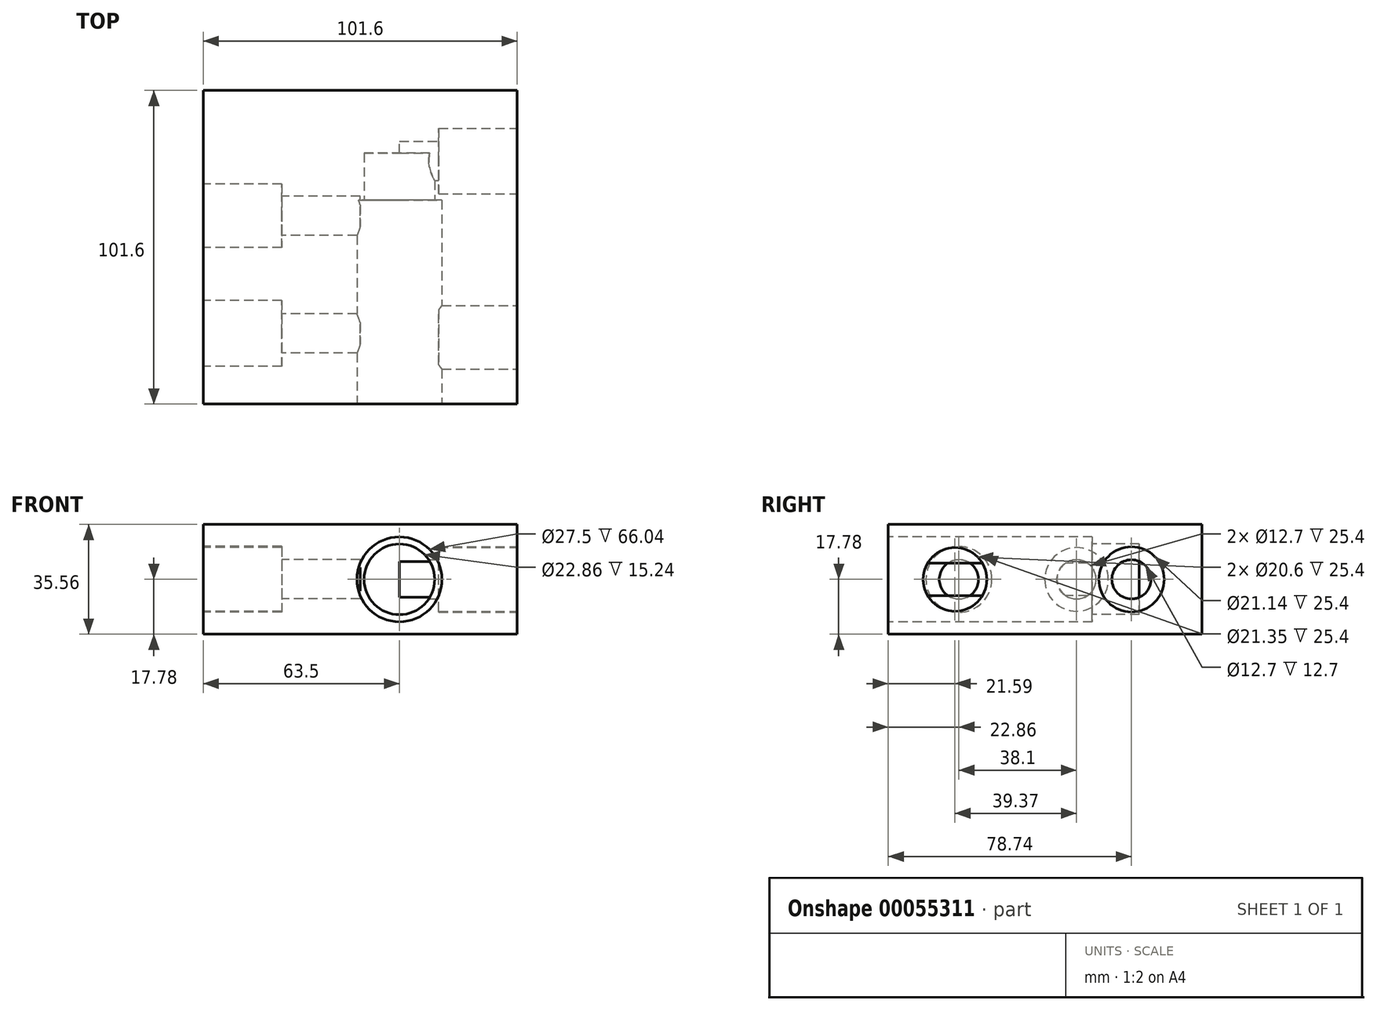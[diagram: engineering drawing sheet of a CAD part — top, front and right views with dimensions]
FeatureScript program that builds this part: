
annotation { "Feature Type Name" : "Feature", "Feature Type Description" : "" }
export const myFeature = defineFeature(function(context is Context, id is Id, definition is map)
    precondition{}
    {
        {
            var Q0;
            Q0=qCreatedBy(makeId("Top.planeOp"),FACE);
            var sketch = newSketch(context, id + "F0", { "sketchPlane" : qUnion([Q0])});
            skLineSegment(sketch, "E0.bottom", {"start": v(0, 0) * mm, "end": v(101.6, 0) * mm});
            skLineSegment(sketch, "E0.top", {"start": v(0, 101.6) * mm, "end": v(101.6, 101.6) * mm});
            skLineSegment(sketch, "E0.left", {"start": v(0, 0) * mm, "end": v(0, 101.6) * mm});
            skLineSegment(sketch, "E0.right", {"start": v(101.6, 0) * mm, "end": v(101.6, 101.6) * mm});
            skSolve(sketch);
        }
        {
            var Q0;
            Q0=makeQuery(id+"F0.imprint","IMPRINT",FACE,{"disambiguationData":[TD([[makeQuery(id+"F0.imprint","IMPRINT",EDGE,{"derivedFrom":sQuery(id+"F0.wireOp",EDGE,"E0.bottom")}),1.0]])]});
            extrude(context, id + "F1", {"entities" : qUnion([Q0]), "depth" : 35.56 * mm});
        }
        {
            var Q0;
            Q0=makeQuery(id+"F1.opExtrude","SWEPT_FACE",FACE,{"disambiguationData":[OSD([sQuery(id+"F0.wireOp",EDGE,"E0.bottom")])]});
            var sketch = newSketch(context, id + "F2", { "sketchPlane" : qUnion([Q0])});
            skCircle(sketch, "E1", {"center": v(63.5, 17.78) * mm, "radius": 13.75 * mm});
            skCircle(sketch, "E2", {"center": v(63.5, 17.78) * mm, "radius": 11.43 * mm});
            skSolve(sketch);
        }
        {
            var Q0;
            Q0=makeQuery(id+"F1.opExtrude","SWEPT_FACE",FACE,{"disambiguationData":[OSD([sQuery(id+"F0.wireOp",EDGE,"E0.left")])]});
            var sketch = newSketch(context, id + "F3", { "sketchPlane" : qUnion([Q0])});
            skCircle(sketch, "E3", {"center": v(-60.96, 17.78) * mm, "radius": 10.3 * mm});
            skCircle(sketch, "E4", {"center": v(-22.86, 17.78) * mm, "radius": 10.68 * mm});
            skCircle(sketch, "E5", {"center": v(-60.96, 17.78) * mm, "radius": 6.35 * mm});
            skCircle(sketch, "E6", {"center": v(-22.86, 17.78) * mm, "radius": 6.35 * mm});
            skSolve(sketch);
        }
        {
            var Q0;
            Q0=makeQuery(id+"F1.opExtrude","SWEPT_FACE",FACE,{"disambiguationData":[OSD([sQuery(id+"F0.wireOp",EDGE,"E0.right")])]});
            var sketch = newSketch(context, id + "F4", { "sketchPlane" : qUnion([Q0])});
            skCircle(sketch, "E7", {"center": v(21.59, 17.78) * mm, "radius": 10.3 * mm});
            skCircle(sketch, "E8", {"center": v(78.74, 17.78) * mm, "radius": 10.57 * mm});
            skCircle(sketch, "E9", {"center": v(78.74, 17.78) * mm, "radius": 6.35 * mm});
            skSolve(sketch);
        }
        {
            var Q0;
            Q0=makeQuery(id+"F2.imprint","IMPRINT",FACE,{"disambiguationData":[TD([[makeQuery(id+"F2.imprint","IMPRINT",EDGE,{"derivedFrom":sQuery(id+"F2.wireOp",EDGE,"E1")}),1.0]])]});
            var Q1;
            Q1=makeQuery(id+"F2.imprint","IMPRINT",FACE,{"disambiguationData":[TD([[makeQuery(id+"F2.imprint","IMPRINT",EDGE,{"derivedFrom":sQuery(id+"F2.wireOp",EDGE,"E2")}),1.0]])]});
            extrude(context, id + "F5", {"entities" : qUnion([Q0, Q1]), "operationType" : NewBodyOperationType.REMOVE, "oppositeDirection" : true, "depth" : 66.04 * mm});
        }
        {
            var Q0;
            Q0=makeQuery(id+"F2.imprint","IMPRINT",FACE,{"disambiguationData":[TD([[makeQuery(id+"F2.imprint","IMPRINT",EDGE,{"derivedFrom":sQuery(id+"F2.wireOp",EDGE,"E2")}),1.0]])]});
            extrude(context, id + "F6", {"entities" : qUnion([Q0]), "operationType" : NewBodyOperationType.REMOVE, "oppositeDirection" : true, "depth" : 81.28 * mm});
        }
        {
            var Q0;
            Q0=makeQuery(id+"F4.imprint","IMPRINT",FACE,{"disambiguationData":[TD([[makeQuery(id+"F4.imprint","IMPRINT",EDGE,{"derivedFrom":sQuery(id+"F4.wireOp",EDGE,"E7")}),1.0]])]});
            var Q1;
            Q1=makeQuery(id+"F4.imprint","IMPRINT",FACE,{"disambiguationData":[TD([[makeQuery(id+"F4.imprint","IMPRINT",EDGE,{"derivedFrom":sQuery(id+"F4.wireOp",EDGE,"E8")}),1.0]])]});
            extrude(context, id + "F7", {"entities" : qUnion([Q0, Q1]), "operationType" : NewBodyOperationType.REMOVE, "oppositeDirection" : true, "depth" : 25.4 * mm});
        }
        {
            var Q0;
            Q0=makeQuery(id+"F3.imprint","IMPRINT",FACE,{"disambiguationData":[TD([[makeQuery(id+"F3.imprint","IMPRINT",EDGE,{"derivedFrom":sQuery(id+"F3.wireOp",EDGE,"E5")}),1.0]])]});
            var Q1;
            Q1=makeQuery(id+"F3.imprint","IMPRINT",FACE,{"disambiguationData":[TD([[makeQuery(id+"F3.imprint","IMPRINT",EDGE,{"derivedFrom":sQuery(id+"F3.wireOp",EDGE,"E6")}),1.0]])]});
            extrude(context, id + "F8", {"entities" : qUnion([Q0, Q1]), "operationType" : NewBodyOperationType.REMOVE, "oppositeDirection" : true, "depth" : 50.8 * mm});
        }
        {
            var Q0;
            Q0=makeQuery(id+"F3.imprint","IMPRINT",FACE,{"disambiguationData":[TD([[makeQuery(id+"F3.imprint","IMPRINT",EDGE,{"derivedFrom":sQuery(id+"F3.wireOp",EDGE,"E3")}),1.0]])]});
            var Q1;
            Q1=makeQuery(id+"F3.imprint","IMPRINT",FACE,{"disambiguationData":[TD([[makeQuery(id+"F3.imprint","IMPRINT",EDGE,{"derivedFrom":sQuery(id+"F3.wireOp",EDGE,"E4")}),1.0]])]});
            extrude(context, id + "F9", {"entities" : qUnion([Q0, Q1]), "operationType" : NewBodyOperationType.REMOVE, "oppositeDirection" : true, "depth" : 25.4 * mm});
        }
        {
            var Q0;
            Q0=makeQuery(id+"F4.imprint","IMPRINT",FACE,{"disambiguationData":[TD([[makeQuery(id+"F4.imprint","IMPRINT",EDGE,{"derivedFrom":sQuery(id+"F4.wireOp",EDGE,"E9")}),1.0]])]});
            extrude(context, id + "F10", {"entities" : qUnion([Q0]), "operationType" : NewBodyOperationType.REMOVE, "oppositeDirection" : true, "depth" : 38.1 * mm});
        }
    });
